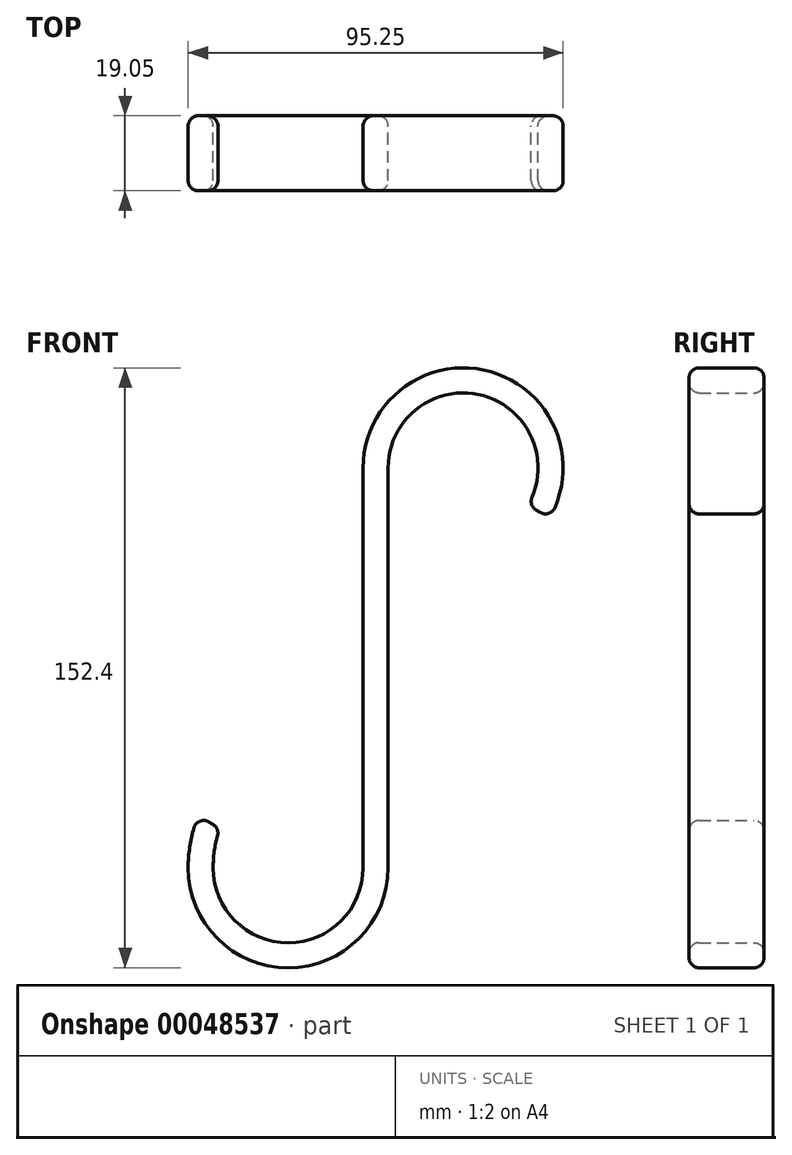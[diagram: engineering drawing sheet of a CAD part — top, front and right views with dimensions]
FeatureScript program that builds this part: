
annotation { "Feature Type Name" : "Feature", "Feature Type Description" : "" }
export const myFeature = defineFeature(function(context is Context, id is Id, definition is map)
    precondition{}
    {
        {
            var Q0;
            Q0=qCreatedBy(makeId("Front.planeOp"),FACE);
            var sketch = newSketch(context, id + "F0", { "sketchPlane" : qUnion([Q0])});
            skLineSegment(sketch, "E0", {"start": v(-36.83, 0) * mm, "end": v(-36.83, -101.6) * mm});
            skArc(sketch, "E1", {"start": v(-36.83, 0) * mm, "mid": v(-11.43, 25.4) * mm, "end": v(13.97, 0) * mm});
            skLineSegment(sketch, "E2", {"start": v(-30.48, 0) * mm, "end": v(-30.48, -101.6) * mm});
            skLineSegment(sketch, "E3", {"start": v(-30.48, 0) * mm, "end": v(-30.48, 0) * mm});
            skArc(sketch, "E4", {"start": v(-30.48, -101.6) * mm, "mid": v(-55.88, -127) * mm, "end": v(-81.28, -101.6) * mm});
            skArc(sketch, "E5", {"start": v(-36.83, -101.6) * mm, "mid": v(-55.88, -120.65) * mm, "end": v(-74.93, -101.6) * mm});
            skLineSegment(sketch, "E6", {"start": v(-11.43, 0) * mm, "end": v(-11.43, -101.6) * mm, "construction": true});
            skLineSegment(sketch, "E7", {"start": v(-55.88, -101.6) * mm, "end": v(-99.9, -76.18) * mm, "construction": true});
            skLineSegment(sketch, "E8", {"start": v(-11.43, 0) * mm, "end": v(23.13, -19.95) * mm, "construction": true});
            skArc(sketch, "E9", {"start": v(-74.93, -101.6) * mm, "mid": v(-74.5, -96.52) * mm, "end": v(-73.24, -91.58) * mm});
            skArc(sketch, "E10", {"start": v(-81.28, -101.6) * mm, "mid": v(-80.64, -94.88) * mm, "end": v(-78.74, -88.4) * mm});
            skLineSegment(sketch, "E11", {"start": v(-78.74, -88.4) * mm, "end": v(-73.24, -91.58) * mm});
            skArc(sketch, "E12", {"start": v(-30.48, 0) * mm, "mid": v(-6.5, 18.4) * mm, "end": v(5.07, -9.52) * mm});
            skArc(sketch, "E13", {"start": v(13.97, 0) * mm, "mid": v(13.1, -6.57) * mm, "end": v(10.57, -12.7) * mm});
            skLineSegment(sketch, "E14", {"start": v(5.07, -9.52) * mm, "end": v(10.57, -12.7) * mm});
            skSolve(sketch);
        }
        {
            var Q0;
            Q0=makeQuery(id+"F0.imprint","IMPRINT",FACE,{"disambiguationData":[TD([[makeQuery(id+"F0.imprint","IMPRINT",EDGE,{"derivedFrom":sQuery(id+"F0.wireOp",EDGE,"E0")}),1.0]])]});
            var Q1;
            Q1=makeQuery(id+"F0.imprint","IMPRINT",FACE,{"disambiguationData":[TD([[makeQuery(id+"F0.imprint","IMPRINT",EDGE,{"derivedFrom":sQuery(id+"F0.wireOp",EDGE,"qGwicptO-gK2j-Kfag-Chg2-fPSLUECn81Ir")}),1.0]])]});
            var Q2;
            Q2=makeQuery(id+"F0.imprint","IMPRINT",FACE,{"disambiguationData":[TD([[makeQuery(id+"F0.imprint","IMPRINT",EDGE,{"derivedFrom":sQuery(id+"F0.wireOp",EDGE,"xNmMEBZU-oUyY-ZiBH-kAaP-bqtLUd6SUk8f")}),1.0]])]});
            extrude(context, id + "F1", {"entities" : qUnion([Q0, Q1, Q2]), "depth" : 19.05 * mm, "offsetDistance" : 25.4 * mm});
        }
        {
            var Q0;
            Q0=makeQuery(id+"F1.opExtrude","SWEPT_FACE",FACE,{"disambiguationData":[OSD([sQuery(id+"F0.wireOp",EDGE,"E11")])]});
            var Q1;
            Q1=makeQuery(id+"F1.opExtrude","SWEPT_FACE",FACE,{"disambiguationData":[OSD([sQuery(id+"F0.wireOp",EDGE,"E14")])]});
            var Q2;
            Q2=makeQuery(id+"F1.opExtrude","CAP_FACE",FACE,{"disambiguationData":[OSD([sQuery(id+"F0.wireOp",EDGE,"E0"),sQuery(id+"F0.wireOp",EDGE,"E1"),sQuery(id+"F0.wireOp",EDGE,"E2"),sQuery(id+"F0.wireOp",EDGE,"E3"),sQuery(id+"F0.wireOp",EDGE,"E4"),sQuery(id+"F0.wireOp",EDGE,"E5"),sQuery(id+"F0.wireOp",EDGE,"E9"),sQuery(id+"F0.wireOp",EDGE,"E10"),sQuery(id+"F0.wireOp",EDGE,"E11"),sQuery(id+"F0.wireOp",EDGE,"E12"),sQuery(id+"F0.wireOp",EDGE,"E13"),sQuery(id+"F0.wireOp",EDGE,"E14")])],"isStart":true});
            var Q3;
            Q3=makeQuery(id+"F1.opExtrude","CAP_FACE",FACE,{"disambiguationData":[OSD([sQuery(id+"F0.wireOp",EDGE,"E0"),sQuery(id+"F0.wireOp",EDGE,"E1"),sQuery(id+"F0.wireOp",EDGE,"E2"),sQuery(id+"F0.wireOp",EDGE,"E3"),sQuery(id+"F0.wireOp",EDGE,"E4"),sQuery(id+"F0.wireOp",EDGE,"E5"),sQuery(id+"F0.wireOp",EDGE,"E9"),sQuery(id+"F0.wireOp",EDGE,"E10"),sQuery(id+"F0.wireOp",EDGE,"E11"),sQuery(id+"F0.wireOp",EDGE,"E12"),sQuery(id+"F0.wireOp",EDGE,"E13"),sQuery(id+"F0.wireOp",EDGE,"E14")])],"isStart":false});
            fillet(context, id + "F2", {"entities" : qUnion([Q0, Q1, Q2, Q3]), "radius" : 2.54 * mm, "tangentPropagation" : true, "allowEdgeOverflow" : false});
        }
    });
